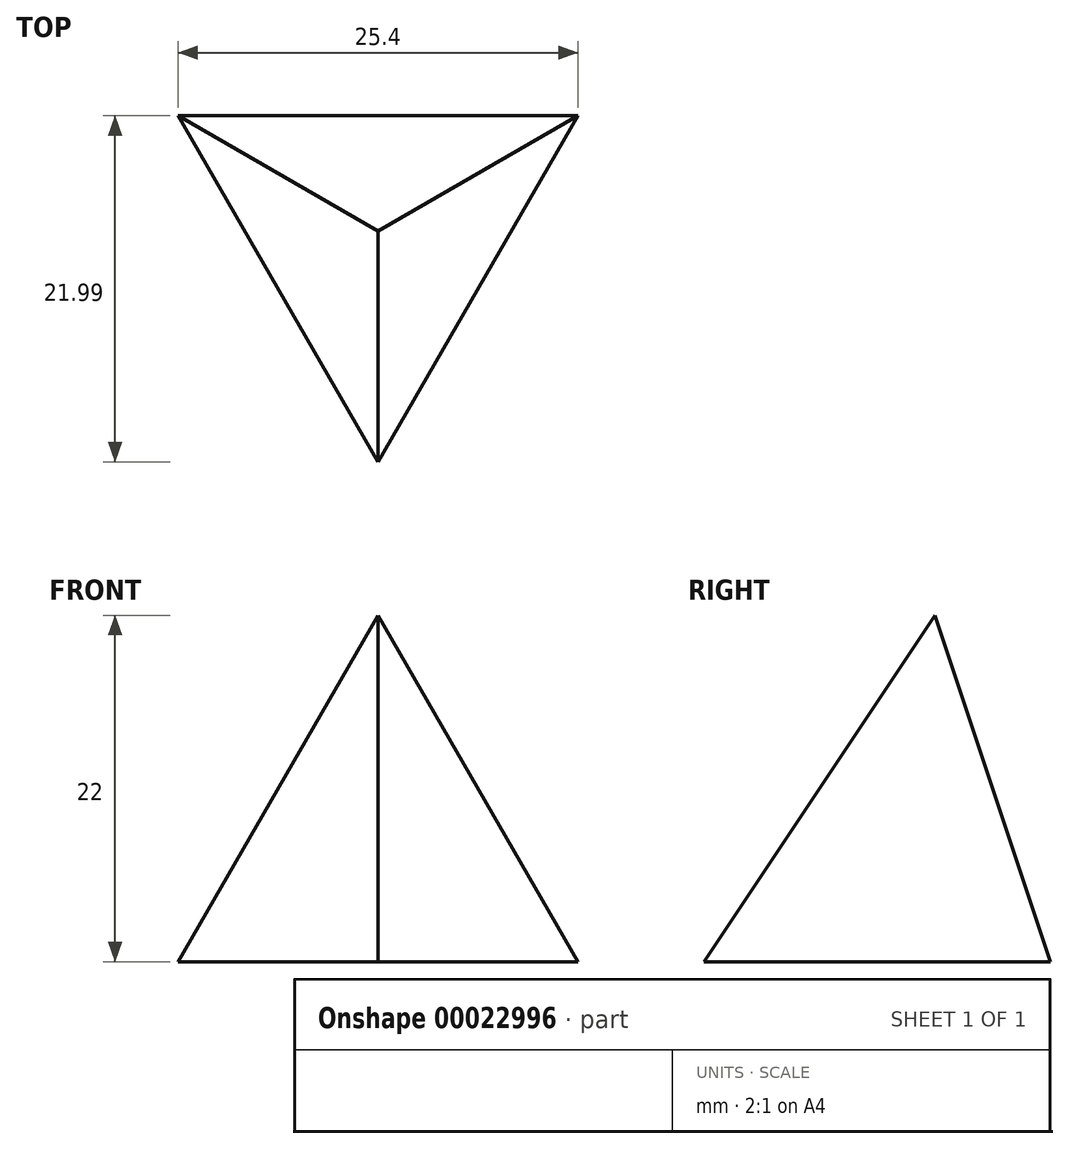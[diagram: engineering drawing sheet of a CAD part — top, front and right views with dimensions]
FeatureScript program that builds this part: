
annotation { "Feature Type Name" : "Feature", "Feature Type Description" : "" }
export const myFeature = defineFeature(function(context is Context, id is Id, definition is map)
    precondition{}
    {
        {
            var Q0;
            Q0=qCreatedBy(makeId("Top.planeOp"),FACE);
            var sketch = newSketch(context, id + "F0", { "sketchPlane" : qUnion([Q0])});
            skCircle(sketch, "E0.cCircle", {"center": v(0, 0) * mm, "radius": 7.33 * mm, "construction": true});
            skLineSegment(sketch, "E0.0", {"start": v(-12.7, 7.33) * mm, "end": v(12.7, 7.33) * mm});
            skLineSegment(sketch, "E0.1", {"start": v(12.7, 7.33) * mm, "end": v(0, -14.66) * mm});
            skLineSegment(sketch, "E0.2", {"start": v(0, -14.66) * mm, "end": v(-12.7, 7.33) * mm});
            skPoint(sketch, "E0.0.midPoint", {"position": v(0, 7.33) * mm});
            skSolve(sketch);
        }
        {
            var Q0;
            Q0=qCreatedBy(makeId("Top.planeOp"),FACE);
            cPlane(context, id + "F1", {"entities" : qUnion([Q0]), "cplaneType" : CPlaneType.OFFSET, "offset" : 22 * mm, "width" : 152.4 * mm, "height" : 152.4 * mm});
        }
        {
            var Q0;
            Q0=qCreatedBy(id+"F1.planeOp",FACE);
            var sketch = newSketch(context, id + "F2", { "sketchPlane" : qUnion([Q0])});
            skPoint(sketch, "E1", {"position": v(0, 0) * mm});
            skSolve(sketch);
        }
        {
            var Q0;
            Q0=makeQuery(id+"F0.imprint","IMPRINT",FACE,{"disambiguationData":[TD([[makeQuery(id+"F0.imprint","IMPRINT",EDGE,{"derivedFrom":sQuery(id+"F0.wireOp",EDGE,"E0.0")}),-1.0]])]});
            var Q1;
            Q1=sQuery(id+"F2.wireOp",VERTEX,"E1");
            loft(context, id + "F3", {"sheetProfilesArray" : [{ "sheetProfileEntities" : qUnion([Q0]) }, { "sheetProfileEntities" : qUnion([Q1]) }]});
        }
    });
